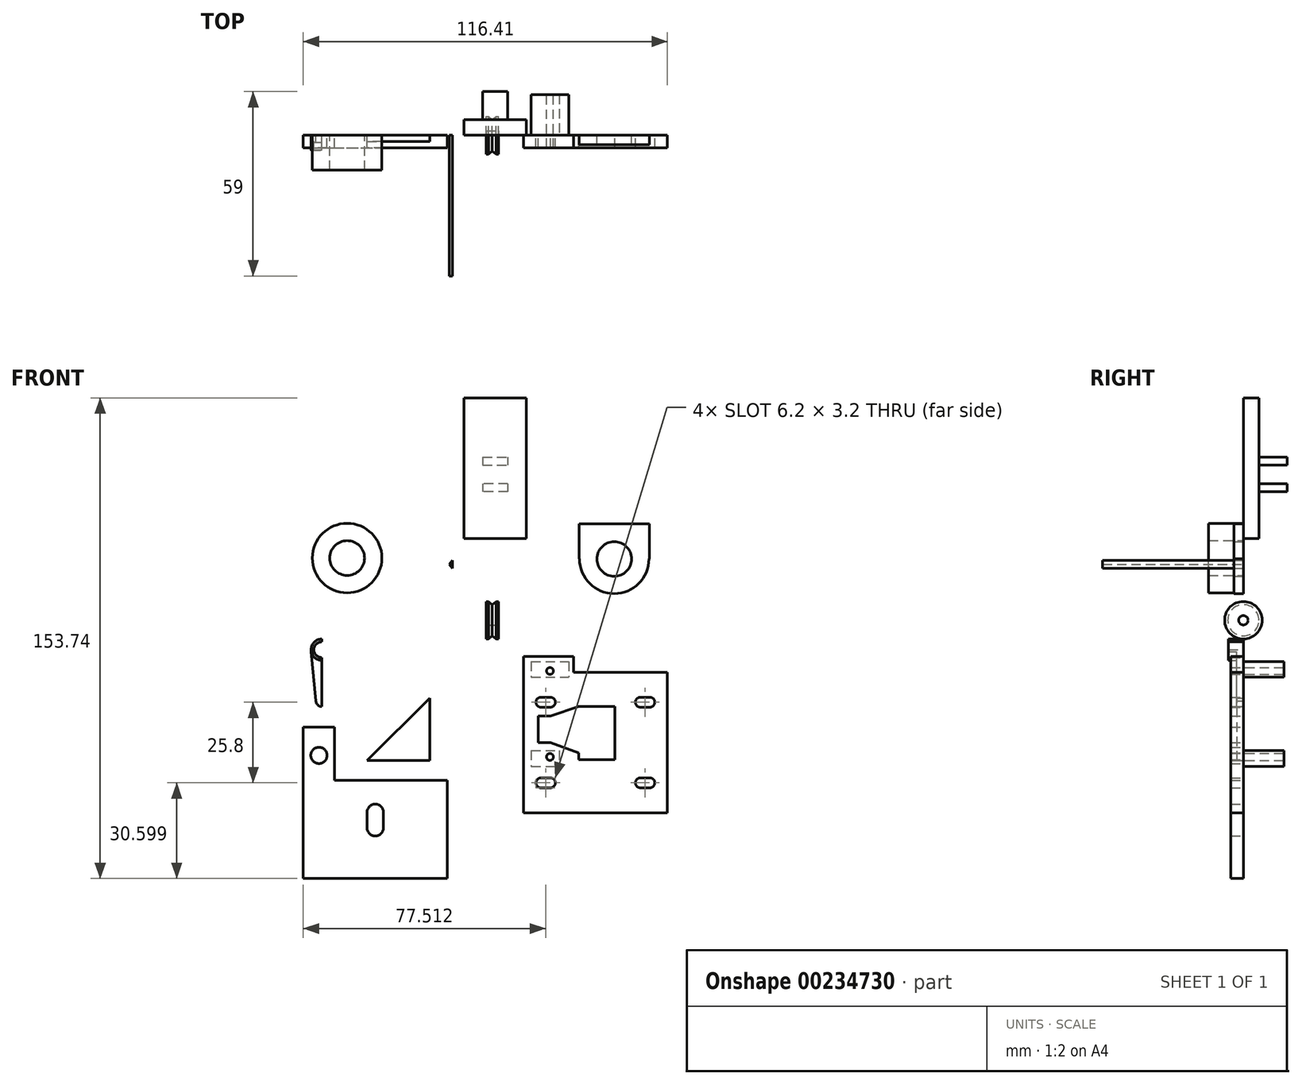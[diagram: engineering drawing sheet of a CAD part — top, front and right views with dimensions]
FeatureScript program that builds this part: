
annotation { "Feature Type Name" : "Feature", "Feature Type Description" : "" }
export const myFeature = defineFeature(function(context is Context, id is Id, definition is map)
    precondition{}
    {
        {
            var Q0;
            Q0=qCreatedBy(makeId("Front.planeOp"),FACE);
            var sketch = newSketch(context, id + "F0", { "sketchPlane" : qUnion([Q0])});
            skCircle(sketch, "E0", {"center": v(-46.42, 28.77) * mm, "radius": 11.12 * mm});
            skCircle(sketch, "E1", {"center": v(-46.42, 28.77) * mm, "radius": 5.55 * mm});
            skCircle(sketch, "E2", {"center": v(-54.55, -0.55) * mm, "radius": 3.4 * mm});
            skCircle(sketch, "E3", {"center": v(-54.55, -0.55) * mm, "radius": 2.5 * mm});
            skCircle(sketch, "E4", {"center": v(-54.55, -16.9) * mm, "radius": 1.85 * mm});
            skLineSegment(sketch, "E5", {"start": v(-57.95, -0.55) * mm, "end": v(-56.4, -16.9) * mm});
            skLineSegment(sketch, "E6", {"start": v(-51.15, -0.55) * mm, "end": v(-52.7, -16.9) * mm});
            skLineSegment(sketch, "E7", {"start": v(-54.55, 2.85) * mm, "end": v(-54.55, -18.75) * mm});
            skLineSegment(sketch, "E8.bottom", {"start": v(9.97, -7.75) * mm, "end": v(55.97, -7.75) * mm});
            skLineSegment(sketch, "E8.top", {"start": v(9.97, -52.75) * mm, "end": v(55.97, -52.75) * mm});
            skLineSegment(sketch, "E8.left", {"start": v(9.97, -7.75) * mm, "end": v(9.97, -52.75) * mm});
            skLineSegment(sketch, "E8.right", {"start": v(55.97, -7.75) * mm, "end": v(55.97, -52.75) * mm});
            skCircle(sketch, "E9", {"center": v(15.57, -17.35) * mm, "radius": 1.6 * mm});
            skCircle(sketch, "E10", {"center": v(18.57, -17.35) * mm, "radius": 1.6 * mm});
            skCircle(sketch, "E11", {"center": v(47.37, -17.35) * mm, "radius": 1.6 * mm});
            skCircle(sketch, "E12", {"center": v(50.37, -17.35) * mm, "radius": 1.6 * mm});
            skLineSegment(sketch, "E13", {"start": v(15.57, -15.75) * mm, "end": v(18.57, -15.75) * mm});
            skLineSegment(sketch, "E14", {"start": v(15.57, -18.95) * mm, "end": v(18.57, -18.95) * mm});
            skLineSegment(sketch, "E15", {"start": v(47.37, -15.75) * mm, "end": v(50.37, -15.75) * mm});
            skLineSegment(sketch, "E16", {"start": v(47.37, -18.95) * mm, "end": v(50.37, -18.95) * mm});
            skPoint(sketch, "E17", {"position": v(13.97, -17.35) * mm});
            skPoint(sketch, "E18", {"position": v(51.97, -17.35) * mm});
            skCircle(sketch, "E19", {"center": v(15.57, -43.15) * mm, "radius": 1.6 * mm});
            skCircle(sketch, "E20", {"center": v(18.57, -43.15) * mm, "radius": 1.6 * mm});
            skCircle(sketch, "E21", {"center": v(47.37, -43.15) * mm, "radius": 1.6 * mm});
            skCircle(sketch, "E22", {"center": v(50.37, -43.15) * mm, "radius": 1.6 * mm});
            skLineSegment(sketch, "E23", {"start": v(15.57, -41.55) * mm, "end": v(18.57, -41.55) * mm});
            skLineSegment(sketch, "E24", {"start": v(15.57, -44.75) * mm, "end": v(18.57, -44.75) * mm});
            skLineSegment(sketch, "E25", {"start": v(47.37, -41.55) * mm, "end": v(50.37, -41.55) * mm});
            skLineSegment(sketch, "E26", {"start": v(47.37, -44.75) * mm, "end": v(50.37, -44.75) * mm});
            skCircle(sketch, "E27", {"center": v(39, 28.47) * mm, "radius": 11.12 * mm});
            skCircle(sketch, "E28", {"center": v(39, 28.47) * mm, "radius": 5.55 * mm});
            skLineSegment(sketch, "E29.bottom", {"start": v(27.73, 39.75) * mm, "end": v(50.28, 39.75) * mm});
            skLineSegment(sketch, "E29.top", {"start": v(27.73, 17.2) * mm, "end": v(50.28, 17.2) * mm});
            skLineSegment(sketch, "E29.left", {"start": v(27.73, 39.75) * mm, "end": v(27.73, 17.2) * mm});
            skLineSegment(sketch, "E29.right", {"start": v(50.28, 39.75) * mm, "end": v(50.28, 17.2) * mm});
            skPoint(sketch, "E30", {"position": v(27.73, 28.47) * mm});
            skPoint(sketch, "E31", {"position": v(50.28, 28.47) * mm});
            skLineSegment(sketch, "E32", {"start": v(27.73, 28.47) * mm, "end": v(50.28, 28.47) * mm});
            skLineSegment(sketch, "E33.bottom", {"start": v(-9.07, 79.99) * mm, "end": v(10.93, 79.99) * mm});
            skLineSegment(sketch, "E33.top", {"start": v(-9.07, 34.99) * mm, "end": v(10.93, 34.99) * mm});
            skLineSegment(sketch, "E33.right", {"start": v(10.93, 79.99) * mm, "end": v(10.93, 34.99) * mm});
            skLineSegment(sketch, "E34.left", {"start": v(4.93, 52.49) * mm, "end": v(4.93, 49.99) * mm});
            skLineSegment(sketch, "E35.bottom", {"start": v(-13.76, 27.96) * mm, "end": v(-12.76, 27.96) * mm});
            skLineSegment(sketch, "E35.top", {"start": v(-13.76, 25.46) * mm, "end": v(-12.76, 25.46) * mm});
            skLineSegment(sketch, "E35.left", {"start": v(-13.76, 27.96) * mm, "end": v(-13.76, 25.46) * mm});
            skLineSegment(sketch, "E35.right", {"start": v(-12.76, 27.96) * mm, "end": v(-12.76, 25.46) * mm});
            skPoint(sketch, "E36", {"position": v(-13.76, 26.71) * mm});
            skLineSegment(sketch, "E37", {"start": v(-12.76, 27.96) * mm, "end": v(-13.76, 26.71) * mm});
            skLineSegment(sketch, "E38", {"start": v(-12.76, 25.46) * mm, "end": v(-13.76, 26.71) * mm});
            skLineSegment(sketch, "E39.bottom", {"start": v(-60.44, -42.35) * mm, "end": v(-14.44, -42.35) * mm});
            skLineSegment(sketch, "E39.top", {"start": v(-60.44, -73.75) * mm, "end": v(-14.44, -73.75) * mm});
            skLineSegment(sketch, "E39.left", {"start": v(-60.44, -42.35) * mm, "end": v(-60.44, -73.75) * mm});
            skLineSegment(sketch, "E39.right", {"start": v(-14.44, -42.35) * mm, "end": v(-14.44, -73.75) * mm});
            skLineSegment(sketch, "E40", {"start": v(-20, -36) * mm, "end": v(-20, -16) * mm});
            skLineSegment(sketch, "E41", {"start": v(-20, -16) * mm, "end": v(-40, -36) * mm});
            skLineSegment(sketch, "E42", {"start": v(-40, -36) * mm, "end": v(-20, -36) * mm});
            skLineSegment(sketch, "E43", {"start": v(-3.07, 52.49) * mm, "end": v(-3.07, 49.99) * mm});
            skLineSegment(sketch, "E44", {"start": v(4.93, 52.49) * mm, "end": v(-3.07, 52.49) * mm});
            skLineSegment(sketch, "E45", {"start": v(4.93, 49.99) * mm, "end": v(-3.07, 49.99) * mm});
            skLineSegment(sketch, "E46.bottom", {"start": v(-3.07, 60.99) * mm, "end": v(4.93, 60.99) * mm});
            skLineSegment(sketch, "E46.top", {"start": v(-3.07, 58.49) * mm, "end": v(4.93, 58.49) * mm});
            skLineSegment(sketch, "E46.left", {"start": v(-3.07, 60.99) * mm, "end": v(-3.07, 58.49) * mm});
            skLineSegment(sketch, "E46.right", {"start": v(4.93, 60.99) * mm, "end": v(4.93, 58.49) * mm});
            skLineSegment(sketch, "E47.bottom", {"start": v(27.7, -18.75) * mm, "end": v(39.2, -18.75) * mm});
            skLineSegment(sketch, "E47.top", {"start": v(27.7, -35.75) * mm, "end": v(39.2, -35.75) * mm});
            skLineSegment(sketch, "E47.left", {"start": v(27.7, -18.75) * mm, "end": v(27.7, -35.75) * mm});
            skLineSegment(sketch, "E47.right", {"start": v(39.2, -18.75) * mm, "end": v(39.2, -35.75) * mm});
            skLineSegment(sketch, "E48.bottom", {"start": v(14.7, -21.75) * mm, "end": v(27.7, -21.75) * mm});
            skLineSegment(sketch, "E48.top", {"start": v(14.7, -30.25) * mm, "end": v(27.7, -30.25) * mm});
            skLineSegment(sketch, "E48.left", {"start": v(14.7, -21.75) * mm, "end": v(14.7, -30.25) * mm});
            skLineSegment(sketch, "E48.right", {"start": v(27.7, -21.75) * mm, "end": v(27.7, -30.25) * mm});
            skLineSegment(sketch, "E49.bottom", {"start": v(9.97, -7.75) * mm, "end": v(25.97, -7.75) * mm});
            skLineSegment(sketch, "E49.top", {"start": v(9.97, -2.75) * mm, "end": v(25.97, -2.75) * mm});
            skLineSegment(sketch, "E49.left", {"start": v(9.97, -7.75) * mm, "end": v(9.97, -2.75) * mm});
            skLineSegment(sketch, "E49.right", {"start": v(25.97, -7.75) * mm, "end": v(25.97, -2.75) * mm});
            skLineSegment(sketch, "E50", {"start": v(-9.07, 79.99) * mm, "end": v(-9.07, 34.99) * mm});
            skLineSegment(sketch, "E51.bottom", {"start": v(12.44, -4.35) * mm, "end": v(24.44, -4.35) * mm});
            skLineSegment(sketch, "E51.top", {"start": v(12.44, -9.35) * mm, "end": v(24.44, -9.35) * mm});
            skLineSegment(sketch, "E51.left", {"start": v(12.44, -4.35) * mm, "end": v(12.44, -9.35) * mm});
            skLineSegment(sketch, "E51.right", {"start": v(24.44, -4.35) * mm, "end": v(24.44, -9.35) * mm});
            skLineSegment(sketch, "E52.bottom", {"start": v(12.44, -32.85) * mm, "end": v(21.44, -32.85) * mm});
            skLineSegment(sketch, "E52.top", {"start": v(12.44, -37.85) * mm, "end": v(21.44, -37.85) * mm});
            skLineSegment(sketch, "E52.left", {"start": v(12.44, -32.85) * mm, "end": v(12.44, -37.85) * mm});
            skLineSegment(sketch, "E52.right", {"start": v(21.44, -32.85) * mm, "end": v(21.44, -37.85) * mm});
            skCircle(sketch, "E53", {"center": v(18.44, -34.85) * mm, "radius": 1.1 * mm});
            skCircle(sketch, "E54", {"center": v(18.44, -7.35) * mm, "radius": 1.1 * mm});
            skLineSegment(sketch, "E55", {"start": v(18.6, -21.75) * mm, "end": v(27.7, -18.75) * mm});
            skLineSegment(sketch, "E56", {"start": v(18.6, -30.25) * mm, "end": v(27.7, -33.53) * mm});
            skCircle(sketch, "E57", {"center": v(-37.44, -57.55) * mm, "radius": 2.6 * mm});
            skPoint(sketch, "E57.centerSnap0", {"position": v(-37.44, -73.75) * mm});
            skCircle(sketch, "E58", {"center": v(-37.44, -52.55) * mm, "radius": 2.6 * mm});
            skLineSegment(sketch, "E59", {"start": v(-40.04, -52.55) * mm, "end": v(-40.04, -57.55) * mm});
            skLineSegment(sketch, "E60", {"start": v(-34.84, -52.55) * mm, "end": v(-34.84, -57.55) * mm});
            skLineSegment(sketch, "E61.bottom", {"start": v(-60.44, -42.35) * mm, "end": v(-50.44, -42.35) * mm});
            skLineSegment(sketch, "E61.top", {"start": v(-60.44, -25.35) * mm, "end": v(-50.44, -25.35) * mm});
            skLineSegment(sketch, "E61.left", {"start": v(-60.44, -42.35) * mm, "end": v(-60.44, -25.35) * mm});
            skLineSegment(sketch, "E61.right", {"start": v(-50.44, -42.35) * mm, "end": v(-50.44, -25.35) * mm});
            skCircle(sketch, "E62", {"center": v(-55.44, -34.35) * mm, "radius": 2.6 * mm});
            skSolve(sketch);
        }
        {
            var Q0;
            Q0=makeQuery(id+"F0.imprint","IMPRINT",FACE,{"disambiguationData":[TD([[makeQuery(id+"F0.imprint","IMPRINT",EDGE,{"derivedFrom":sQuery(id+"F0.wireOp",EDGE,"E0")}),1.0]])]});
            extrude(context, id + "F1", {"entities" : qUnion([Q0]), "depth" : 11.1 * mm, "offsetDistance" : 25 * mm});
        }
        {
            var Q0;
            Q0=qCreatedBy(makeId("Front.planeOp"),FACE);
            var sketch = newSketch(context, id + "F2", { "sketchPlane" : qUnion([Q0])});
            skLineSegment(sketch, "E63.bottom", {"start": v(2, 8.86) * mm, "end": v(-2, 8.86) * mm});
            skLineSegment(sketch, "E63.top", {"start": v(2, 14.86) * mm, "end": v(-2, 14.86) * mm});
            skLineSegment(sketch, "E63.left", {"start": v(2, 8.86) * mm, "end": v(2, 14.86) * mm});
            skLineSegment(sketch, "E63.right", {"start": v(-2, 8.86) * mm, "end": v(-2, 14.86) * mm});
            skPoint(sketch, "E63.middle", {"position": v(0, 11.86) * mm});
            skLineSegment(sketch, "E64", {"start": v(-1.25, 14.86) * mm, "end": v(0, 13.86) * mm});
            skPoint(sketch, "E64.endSnap0", {"position": v(0, 14.86) * mm});
            skLineSegment(sketch, "E65", {"start": v(0, 13.86) * mm, "end": v(1.25, 14.86) * mm});
            skLineSegment(sketch, "E66", {"start": v(-2, 10.36) * mm, "end": v(2, 10.36) * mm});
            skSolve(sketch);
        }
        {
            var Q0;
            {var subQ7=sQuery(id+"F2.wireOp",EDGE,"E64");Q0=makeQuery(id+"F2.imprint","IMPRINT",FACE,{"disambiguationData":[TD([[makeQuery(id+"F2.imprint","IMPRINT",EDGE,{"derivedFrom":subQ7}),-1.0]])]});}
            var Q1;
            Q1=sQuery(id+"F2.wireOp",EDGE,"E63.bottom");
            revolve(context, id + "F3", {"surfaceOperationType" : NewSurfaceOperationType.NEW, "entities" : qUnion([Q0]), "axis" : qUnion([Q1]), "revolveType" : RevolveType.FULL});
        }
        {
            var Q0;
            {var subQ1=sQuery(id+"F0.wireOp",EDGE,"E2");var subQ4=sQuery(id+"F0.wireOp",EDGE,"E7");var subQ9=makeQuery(id+"F0.imprint","INTERSECT",VERTEX,{"disambiguationData":[OD(1.0)],"derivedFrom":[subQ1,subQ4]});Q0=makeQuery(id+"F0.imprint","IMPRINT",FACE,{"disambiguationData":[TD([[makeQuery(id+"F0.imprint","IMPRINT",EDGE,{"disambiguationData":[TD([[subQ9,-1.0]])],"derivedFrom":subQ1}),1.0]])]});}
            var Q1;
            {var subQ0=sQuery(id+"F0.wireOp",EDGE,"E3");var subQ1=makeQuery(id+"F0.imprint","IMPRINT",VERTEX,{"derivedFrom":subQ0});Q1=makeQuery(id+"F0.imprint","IMPRINT",FACE,{"disambiguationData":[TD([[makeQuery(id+"F0.imprint","IMPRINT",EDGE,{"disambiguationData":[TD([[subQ1,1.0]])],"derivedFrom":subQ0}),-1.0]])]});}
            extrude(context, id + "F4", {"entities" : qUnion([Q0, Q1]), "depth" : 4.8 * mm, "offsetDistance" : 25 * mm});
        }
        {
            var Q0;
            {var subQ0=sQuery(id+"F0.wireOp",EDGE,"E5");var subQ1=sQuery(id+"F0.wireOp",EDGE,"E2");var subQ2=makeQuery(id+"F0.imprint","INTERSECT",VERTEX,{"disambiguationData":[OD(0.0)],"derivedFrom":[subQ1,subQ0]});Q0=makeQuery(id+"F0.imprint","IMPRINT",FACE,{"disambiguationData":[TD([[makeQuery(id+"F0.imprint","IMPRINT",EDGE,{"disambiguationData":[TD([[subQ2,-1.0]])],"derivedFrom":subQ1}),-1.0]])]});}
            var Q1;
            {var subQ3=sQuery(id+"F0.wireOp",EDGE,"E4");var subQ5=makeQuery(id+"F0.imprint","IMPRINT",VERTEX,{"derivedFrom":subQ3});Q1=makeQuery(id+"F0.imprint","IMPRINT",FACE,{"disambiguationData":[TD([[makeQuery(id+"F0.imprint","IMPRINT",EDGE,{"disambiguationData":[TD([[subQ5,1.0]])],"derivedFrom":subQ3}),-1.0]])]});}
            var Q2;
            {var subQ0=sQuery(id+"F0.wireOp",EDGE,"E4");var subQ4=makeQuery(id+"F0.imprint","IMPRINT",VERTEX,{"derivedFrom":subQ0});Q2=makeQuery(id+"F0.imprint","IMPRINT",FACE,{"disambiguationData":[TD([[makeQuery(id+"F0.imprint","IMPRINT",EDGE,{"disambiguationData":[TD([[subQ4,1.0]])],"derivedFrom":subQ0}),1.0]])]});}
            var Q3;
            {var subQ0=sQuery(id+"F0.wireOp",EDGE,"E4");var subQ1=makeQuery(id+"F0.imprint","INTERSECT",VERTEX,{"derivedFrom":[subQ0,sQuery(id+"F0.wireOp",EDGE,"E5")]});Q3=makeQuery(id+"F0.imprint","IMPRINT",FACE,{"disambiguationData":[TD([[makeQuery(id+"F0.imprint","IMPRINT",EDGE,{"disambiguationData":[TD([[subQ1,1.0]])],"derivedFrom":subQ0}),1.0]])]});}
            extrude(context, id + "F5", {"entities" : qUnion([Q0, Q1, Q2, Q3]), "operationType" : NewBodyOperationType.ADD, "depth" : 2.2 * mm, "offsetDistance" : 25 * mm});
        }
        {
            var Q0;
            Q0=makeQuery(id+"F0.imprint","IMPRINT",FACE,{"disambiguationData":[TD([[makeQuery(id+"F0.imprint","IMPRINT",EDGE,{"derivedFrom":sQuery(id+"F0.wireOp",EDGE,"E49.top")}),-1.0]])]});
            var Q1;
            {var subQ0=sQuery(id+"F0.wireOp",EDGE,"E51.bottom");Q1=makeQuery(id+"F0.imprint","IMPRINT",FACE,{"disambiguationData":[TD([[makeQuery(id+"F0.imprint","IMPRINT",EDGE,{"derivedFrom":subQ0}),-1.0]])]});}
            var Q2;
            {var subQ0=sQuery(id+"F0.wireOp",EDGE,"E51.top");Q2=makeQuery(id+"F0.imprint","IMPRINT",FACE,{"disambiguationData":[TD([[makeQuery(id+"F0.imprint","IMPRINT",EDGE,{"derivedFrom":subQ0}),1.0]])]});}
            var Q3;
            Q3=makeQuery(id+"F0.imprint","IMPRINT",FACE,{"disambiguationData":[TD([[makeQuery(id+"F0.imprint","IMPRINT",EDGE,{"derivedFrom":sQuery(id+"F0.wireOp",EDGE,"E8.top")}),1.0]])]});
            var Q4;
            Q4=makeQuery(id+"F0.imprint","IMPRINT",FACE,{"disambiguationData":[TD([[makeQuery(id+"F0.imprint","IMPRINT",EDGE,{"derivedFrom":sQuery(id+"F0.wireOp",EDGE,"E52.bottom")}),-1.0]])]});
            extrude(context, id + "F6", {"entities" : qUnion([Q0, Q1, Q2, Q3, Q4]), "depth" : 4 * mm, "offsetDistance" : 25 * mm});
        }
        {
            var Q0;
            {var subQ0=sQuery(id+"F0.wireOp",EDGE,"E32");var subQ1=sQuery(id+"F0.wireOp",EDGE,"E27");var subQ2=makeQuery(id+"F0.imprint","INTERSECT",VERTEX,{"disambiguationData":[OD(0.0)],"derivedFrom":[subQ1,subQ0]});Q0=makeQuery(id+"F0.imprint","IMPRINT",FACE,{"disambiguationData":[TD([[makeQuery(id+"F0.imprint","IMPRINT",EDGE,{"disambiguationData":[TD([[subQ2,1.0]])],"derivedFrom":subQ1}),1.0]])]});}
            var Q1;
            {var subQ1=sQuery(id+"F0.wireOp",EDGE,"E29.bottom");Q1=makeQuery(id+"F0.imprint","IMPRINT",FACE,{"disambiguationData":[TD([[makeQuery(id+"F0.imprint","IMPRINT",EDGE,{"derivedFrom":subQ1}),-1.0]])]});}
            var Q2;
            {var subQ0=sQuery(id+"F0.wireOp",EDGE,"E32");var subQ1=sQuery(id+"F0.wireOp",EDGE,"E27");var subQ2=makeQuery(id+"F0.imprint","INTERSECT",VERTEX,{"disambiguationData":[OD(0.0)],"derivedFrom":[subQ1,subQ0]});Q2=makeQuery(id+"F0.imprint","IMPRINT",FACE,{"disambiguationData":[TD([[makeQuery(id+"F0.imprint","IMPRINT",EDGE,{"disambiguationData":[TD([[subQ2,-1.0]])],"derivedFrom":subQ1}),1.0]])]});}
            extrude(context, id + "F7", {"entities" : qUnion([Q0, Q1, Q2]), "depth" : 3 * mm, "offsetDistance" : 25 * mm});
        }
        {
            var Q0;
            Q0=makeQuery(id+"F0.imprint","IMPRINT",FACE,{"disambiguationData":[TD([[makeQuery(id+"F0.imprint","IMPRINT",EDGE,{"derivedFrom":sQuery(id+"F0.wireOp",EDGE,"E33.bottom")}),-1.0]])]});
            extrude(context, id + "F8", {"entities" : qUnion([Q0]), "depth" : -5 * mm, "offsetDistance" : 25 * mm});
        }
        {
            var Q0;
            Q0=makeQuery(id+"F0.imprint","IMPRINT",FACE,{"disambiguationData":[TD([[makeQuery(id+"F0.imprint","IMPRINT",EDGE,{"derivedFrom":sQuery(id+"F0.wireOp",EDGE,"E46.bottom")}),-1.0]])]});
            var Q1;
            Q1=makeQuery(id+"F0.imprint","IMPRINT",FACE,{"disambiguationData":[TD([[makeQuery(id+"F0.imprint","IMPRINT",EDGE,{"derivedFrom":sQuery(id+"F0.wireOp",EDGE,"E34.left")}),-1.0]])]});
            extrude(context, id + "F9", {"entities" : qUnion([Q0, Q1]), "operationType" : NewBodyOperationType.ADD, "depth" : -14 * mm, "offsetDistance" : 25 * mm});
        }
        {
            var Q0;
            Q0=makeQuery(id+"F0.imprint","IMPRINT",FACE,{"disambiguationData":[TD([[makeQuery(id+"F0.imprint","IMPRINT",EDGE,{"derivedFrom":sQuery(id+"F0.wireOp",EDGE,"E35.right")}),-1.0]])]});
            extrude(context, id + "F10", {"entities" : qUnion([Q0]), "depth" : 45 * mm, "offsetDistance" : 25 * mm});
        }
        {
            var Q0;
            Q0=makeQuery(id+"F0.imprint","IMPRINT",FACE,{"disambiguationData":[TD([[makeQuery(id+"F0.imprint","IMPRINT",EDGE,{"derivedFrom":sQuery(id+"F0.wireOp",EDGE,"E39.bottom")}),-1.0]])]});
            var Q1;
            Q1=makeQuery(id+"F0.imprint","IMPRINT",FACE,{"disambiguationData":[TD([[makeQuery(id+"F0.imprint","IMPRINT",EDGE,{"derivedFrom":sQuery(id+"F0.wireOp",EDGE,"E61.top")}),-1.0]])]});
            extrude(context, id + "F11", {"entities" : qUnion([Q0, Q1]), "depth" : 4 * mm, "offsetDistance" : 25 * mm});
        }
        {
            var Q0;
            Q0=makeQuery(id+"F0.imprint","IMPRINT",FACE,{"disambiguationData":[TD([[makeQuery(id+"F0.imprint","IMPRINT",EDGE,{"derivedFrom":sQuery(id+"F0.wireOp",EDGE,"E40")}),1.0]])]});
            extrude(context, id + "F12", {"entities" : qUnion([Q0]), "depth" : 2 * mm, "offsetDistance" : 25 * mm});
        }
        {
            var Q0;
            {var subQ5=sQuery(id+"F0.wireOp",EDGE,"E51.bottom");Q0=makeQuery(id+"F0.imprint","IMPRINT",FACE,{"disambiguationData":[TD([[makeQuery(id+"F0.imprint","IMPRINT",EDGE,{"derivedFrom":subQ5}),-1.0]])]});}
            var Q1;
            {var subQ5=sQuery(id+"F0.wireOp",EDGE,"E51.top");Q1=makeQuery(id+"F0.imprint","IMPRINT",FACE,{"disambiguationData":[TD([[makeQuery(id+"F0.imprint","IMPRINT",EDGE,{"derivedFrom":subQ5}),1.0]])]});}
            var Q2;
            Q2=makeQuery(id+"F0.imprint","IMPRINT",FACE,{"disambiguationData":[TD([[makeQuery(id+"F0.imprint","IMPRINT",EDGE,{"derivedFrom":sQuery(id+"F0.wireOp",EDGE,"E52.bottom")}),-1.0]])]});
            extrude(context, id + "F13", {"entities" : qUnion([Q0, Q1, Q2]), "operationType" : NewBodyOperationType.ADD, "depth" : -13 * mm, "offsetDistance" : 25 * mm});
        }
    });
